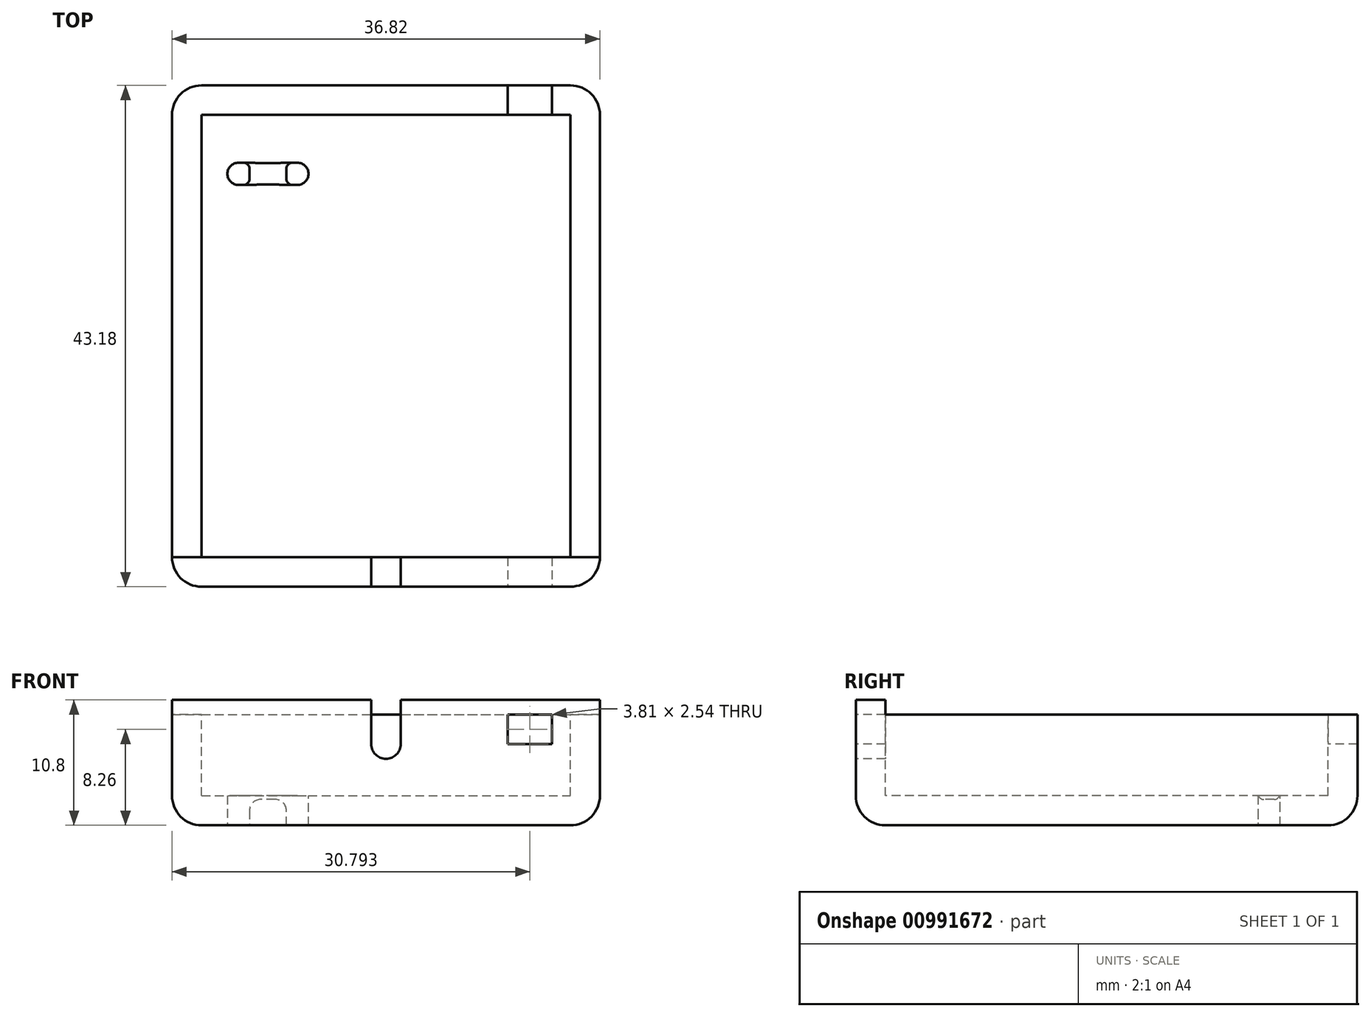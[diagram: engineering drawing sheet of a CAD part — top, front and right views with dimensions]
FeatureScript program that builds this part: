
annotation { "Feature Type Name" : "Feature", "Feature Type Description" : "" }
export const myFeature = defineFeature(function(context is Context, id is Id, definition is map)
    precondition{}
    {
        {
            var Q0;
            Q0=qCreatedBy(makeId("Top.planeOp"),FACE);
            var sketch = newSketch(context, id + "F0", { "sketchPlane" : qUnion([Q0])});
            skLineSegment(sketch, "E0.bottom", {"start": v(-18.42, 21.59) * mm, "end": v(18.42, 21.59) * mm});
            skLineSegment(sketch, "E0.top", {"start": v(-18.42, -21.6) * mm, "end": v(18.42, -21.6) * mm});
            skLineSegment(sketch, "E0.left", {"start": v(-18.42, 21.59) * mm, "end": v(-18.42, -21.6) * mm});
            skLineSegment(sketch, "E0.right", {"start": v(18.42, 21.59) * mm, "end": v(18.42, -21.6) * mm});
            skPoint(sketch, "E0.middle", {"position": v(0, 0) * mm});
            skSolve(sketch);
        }
        {
            var Q0;
            Q0 = qSketchRegion(id + "F0", true);
            extrude(context, id + "F1", {"entities" : qUnion([Q0]), "oppositeDirection" : true, "depth" : 9.52 * mm, "offsetDistance" : 25.4 * mm});
        }
        {
            var Q0;
            Q0=makeQuery(id+"F1.opExtrude","CAP_FACE",FACE,{"disambiguationData":[OSD([sQuery(id+"F0.wireOp",EDGE,"E0.bottom"),sQuery(id+"F0.wireOp",EDGE,"E0.top"),sQuery(id+"F0.wireOp",EDGE,"E0.left"),sQuery(id+"F0.wireOp",EDGE,"E0.right")])],"isStart":true});
            shell(context, id + "F2", {"entities" : qUnion([Q0]), "thickness" : 2.54 * mm});
        }
        {
            var Q0;
            Q0=makeQuery(id+"F1.opExtrude","CAP_FACE",FACE,{"disambiguationData":[OSD([sQuery(id+"F0.wireOp",EDGE,"E0.bottom"),sQuery(id+"F0.wireOp",EDGE,"E0.top"),sQuery(id+"F0.wireOp",EDGE,"E0.left"),sQuery(id+"F0.wireOp",EDGE,"E0.right")])],"isStart":true});
            var sketch = newSketch(context, id + "F3", { "sketchPlane" : qUnion([Q0])});
            skLineSegment(sketch, "E1.bottom", {"start": v(-18.42, -21.6) * mm, "end": v(18.42, -21.6) * mm});
            skLineSegment(sketch, "E1.top", {"start": v(-18.42, -19.05) * mm, "end": v(18.42, -19.05) * mm});
            skLineSegment(sketch, "E1.left", {"start": v(-18.42, -21.6) * mm, "end": v(-18.42, -19.05) * mm});
            skLineSegment(sketch, "E1.right", {"start": v(18.42, -21.6) * mm, "end": v(18.42, -19.05) * mm});
            skSolve(sketch);
        }
        {
            var Q0;
            Q0 = qSketchRegion(id + "F3", true);
            extrude(context, id + "F4", {"entities" : qUnion([Q0]), "operationType" : NewBodyOperationType.ADD, "depth" : 1.27 * mm, "offsetDistance" : 25.4 * mm});
        }
        {
            var Q0;
            Q0=makeQuery(id+"F4.boolean.opBoolean","MERGE",FACE,{"derivedFrom":[makeQuery(id+"F1.opExtrude","SWEPT_FACE",FACE,{"disambiguationData":[OSD([sQuery(id+"F0.wireOp",EDGE,"E0.top")])]}),makeQuery(id+"F4.opExtrude","SWEPT_FACE",FACE,{"disambiguationData":[OSD([sQuery(id+"F3.wireOp",EDGE,"E1.bottom")])]})]});
            var sketch = newSketch(context, id + "F5", { "sketchPlane" : qUnion([Q0])});
            skLineSegment(sketch, "E2", {"start": v(0, 1.27) * mm, "end": v(0, 0) * mm, "construction": true});
            skPoint(sketch, "E2.endSnap0", {"position": v(0, 1.27) * mm});
            skLineSegment(sketch, "E3", {"start": v(-10.48, 0) * mm, "end": v(10.48, 0) * mm, "construction": true});
            skLineSegment(sketch, "E4.bottom", {"start": v(10.48, 0) * mm, "end": v(14.29, 0) * mm});
            skLineSegment(sketch, "E4.top", {"start": v(10.48, -2.54) * mm, "end": v(14.29, -2.54) * mm});
            skLineSegment(sketch, "E4.left", {"start": v(10.48, 0) * mm, "end": v(10.48, -2.54) * mm});
            skLineSegment(sketch, "E4.right", {"start": v(14.29, 0) * mm, "end": v(14.29, -2.54) * mm});
            skSolve(sketch);
        }
        {
            var Q0;
            Q0=makeQuery(id+"F5.imprint","IMPRINT",FACE,{"disambiguationData":[TD([[makeQuery(id+"F5.imprint","IMPRINT",EDGE,{"derivedFrom":sQuery(id+"F5.wireOp",EDGE,"E4.bottom")}),-1.0]])]});
            extrude(context, id + "F6", {"entities" : qUnion([Q0]), "operationType" : NewBodyOperationType.REMOVE, "endBound" : BoundingType.THROUGH_ALL, "oppositeDirection" : true, "depth" : 25.4 * mm, "offsetDistance" : 25.4 * mm});
        }
        {
            var Q0;
            Q0=makeQuery(id+"F4.boolean.opBoolean","MERGE",EDGE,{"derivedFrom":[makeQuery(id+"F1.opExtrude","SWEPT_EDGE",EDGE,{"disambiguationData":[OSD([sQuery(id+"F0.wireOp",EDGE,"E0.top"),sQuery(id+"F0.wireOp",EDGE,"E0.right")])]}),makeQuery(id+"F4.opExtrude","SWEPT_EDGE",EDGE,{"disambiguationData":[OSD([sQuery(id+"F3.wireOp",EDGE,"E1.bottom"),sQuery(id+"F3.wireOp",EDGE,"E1.right")])]})]});
            var Q1;
            Q1=makeQuery(id+"F1.opExtrude","CAP_EDGE",EDGE,{"disambiguationData":[OSD([sQuery(id+"F0.wireOp",EDGE,"E0.right")])],"isStart":false});
            var Q2;
            Q2=makeQuery(id+"F1.opExtrude","CAP_EDGE",EDGE,{"disambiguationData":[OSD([sQuery(id+"F0.wireOp",EDGE,"E0.top")])],"isStart":false});
            var Q3;
            Q3=makeQuery(id+"F4.boolean.opBoolean","MERGE",EDGE,{"derivedFrom":[makeQuery(id+"F1.opExtrude","SWEPT_EDGE",EDGE,{"disambiguationData":[OSD([sQuery(id+"F0.wireOp",EDGE,"E0.top"),sQuery(id+"F0.wireOp",EDGE,"E0.left")])]}),makeQuery(id+"F4.opExtrude","SWEPT_EDGE",EDGE,{"disambiguationData":[OSD([sQuery(id+"F3.wireOp",EDGE,"E1.bottom"),sQuery(id+"F3.wireOp",EDGE,"E1.left")])]})]});
            var Q4;
            Q4=makeQuery(id+"F1.opExtrude","CAP_EDGE",EDGE,{"disambiguationData":[OSD([sQuery(id+"F0.wireOp",EDGE,"E0.left")])],"isStart":false});
            var Q5;
            Q5=makeQuery(id+"F3Qj1YdDXKK0PNa_1.1.F4.boolean.opBoolean","MERGE",EDGE,{"derivedFrom":[makeQuery(id+"F1.opExtrude","SWEPT_EDGE",EDGE,{"disambiguationData":[OSD([sQuery(id+"F0.wireOp",EDGE,"E0.bottom"),sQuery(id+"F0.wireOp",EDGE,"E0.left")])]}),makeQuery(id+"F3Qj1YdDXKK0PNa_1.1.F4.opExtrude","SWEPT_EDGE",EDGE,{"disambiguationData":[OSD([sQuery(id+"F3.wireOp",EDGE,"E1.bottom"),sQuery(id+"F3.wireOp",EDGE,"E1.left")])]})]});
            var Q6;
            Q6=makeQuery(id+"F3Qj1YdDXKK0PNa_1.1.F4.boolean.opBoolean","MERGE",EDGE,{"derivedFrom":[makeQuery(id+"F1.opExtrude","SWEPT_EDGE",EDGE,{"disambiguationData":[OSD([sQuery(id+"F0.wireOp",EDGE,"E0.bottom"),sQuery(id+"F0.wireOp",EDGE,"E0.left")])]}),makeQuery(id+"F3Qj1YdDXKK0PNa_1.1.F4.opExtrude","SWEPT_EDGE",EDGE,{"disambiguationData":[OSD([sQuery(id+"F3.wireOp",EDGE,"E1.bottom"),sQuery(id+"F3.wireOp",EDGE,"E1.left")])]})]});
            var Q7;
            Q7=makeQuery(id+"F1.opExtrude","CAP_EDGE",EDGE,{"disambiguationData":[OSD([sQuery(id+"F0.wireOp",EDGE,"E0.bottom")])],"isStart":false});
            var Q8;
            Q8=makeQuery(id+"F3Qj1YdDXKK0PNa_1.1.F4.boolean.opBoolean","MERGE",EDGE,{"derivedFrom":[makeQuery(id+"F1.opExtrude","SWEPT_EDGE",EDGE,{"disambiguationData":[OSD([sQuery(id+"F0.wireOp",EDGE,"E0.bottom"),sQuery(id+"F0.wireOp",EDGE,"E0.right")])]}),makeQuery(id+"F3Qj1YdDXKK0PNa_1.1.F4.opExtrude","SWEPT_EDGE",EDGE,{"disambiguationData":[OSD([sQuery(id+"F3.wireOp",EDGE,"E1.bottom"),sQuery(id+"F3.wireOp",EDGE,"E1.right")])]})]});
            fillet(context, id + "F7", {"entities" : qUnion([Q0, Q1, Q2, Q3, Q4, Q5, Q6, Q7, Q8]), "radius" : 2.54 * mm, "tangentPropagation" : true, "allowEdgeOverflow" : false});
        }
        {
            var Q0;
            Q0=makeQuery(id+"F4.boolean.opBoolean","MERGE",FACE,{"derivedFrom":[makeQuery(id+"F1.opExtrude","SWEPT_FACE",FACE,{"disambiguationData":[OSD([sQuery(id+"F0.wireOp",EDGE,"E0.top")])]}),makeQuery(id+"F4.opExtrude","SWEPT_FACE",FACE,{"disambiguationData":[OSD([sQuery(id+"F3.wireOp",EDGE,"E1.bottom")])]})]});
            var sketch = newSketch(context, id + "F8", { "sketchPlane" : qUnion([Q0])});
            skLineSegment(sketch, "E5.bottom", {"start": v(-1.27, 1.27) * mm, "end": v(1.27, 1.27) * mm});
            skLineSegment(sketch, "E5.top", {"start": v(-1.27, -2.54) * mm, "end": v(1.27, -2.54) * mm, "construction": true});
            skLineSegment(sketch, "E5.left", {"start": v(-1.27, 1.27) * mm, "end": v(-1.27, -2.54) * mm});
            skLineSegment(sketch, "E5.right", {"start": v(1.27, 1.27) * mm, "end": v(1.27, -2.54) * mm});
            skArc(sketch, "E6", {"start": v(1.27, -2.54) * mm, "mid": v(0, -3.81) * mm, "end": v(-1.27, -2.54) * mm});
            skLineSegment(sketch, "E7", {"start": v(0, 1.27) * mm, "end": v(0, 0) * mm, "construction": true});
            skLineSegment(sketch, "E8", {"start": v(1.27, -2.54) * mm, "end": v(10.48, -2.54) * mm, "construction": true});
            skSolve(sketch);
        }
        {
            var Q0;
            Q0 = qSketchRegion(id + "F8", true);
            extrude(context, id + "F9", {"entities" : qUnion([Q0]), "operationType" : NewBodyOperationType.REMOVE, "endBound" : BoundingType.UP_TO_NEXT, "oppositeDirection" : true, "depth" : 25.4 * mm, "offsetDistance" : 25.4 * mm});
        }
        {
            var Q0;
            Q0=makeQuery(id+"F3Qj1YdDXKK0PNa_1.1.F4.boolean.opBoolean","MERGE",FACE,{"derivedFrom":[makeQuery(id+"F2.opShell","OFFSET_FACE",FACE,{"disambiguationData":[OSD([sQuery(id+"F0.wireOp",EDGE,"E0.bottom")])]}),makeQuery(id+"F3Qj1YdDXKK0PNa_1.1.F4.opExtrude","SWEPT_FACE",FACE,{"disambiguationData":[OSD([sQuery(id+"F3.wireOp",EDGE,"E1.top")])]})]});
            cPlane(context, id + "F10", {"entities" : qUnion([Q0]), "cplaneType" : CPlaneType.OFFSET, "offset" : 5.08 * mm, "width" : 152.4 * mm, "height" : 152.4 * mm});
        }
        {
            var Q0;
            Q0=qCreatedBy(id+"F10.planeOp",FACE);
            var sketch = newSketch(context, id + "F11", { "sketchPlane" : qUnion([Q0])});
            skLineSegment(sketch, "E9.0", {"start": v(-15.88, -6.99) * mm, "end": v(15.88, -6.99) * mm, "construction": true});
            skLineSegment(sketch, "E10.0", {"start": v(-15.88, -9.53) * mm, "end": v(15.88, -9.53) * mm, "construction": true});
            skLineSegment(sketch, "E11", {"start": v(-7.62, -9.53) * mm, "end": v(-7.62, -8.26) * mm});
            skLineSegment(sketch, "E12", {"start": v(-12.7, -9.53) * mm, "end": v(-12.7, -8.26) * mm});
            skLineSegment(sketch, "E13", {"start": v(0, -6.99) * mm, "end": v(0, -13.56) * mm, "construction": true});
            skLineSegment(sketch, "E14", {"start": v(0, -13.56) * mm, "end": v(-10.16, -13.56) * mm, "construction": true});
            skLineSegment(sketch, "E15", {"start": v(-9.53, -6.35) * mm, "end": v(-10.8, -6.35) * mm});
            skArc(sketch, "E16", {"start": v(-7.62, -8.26) * mm, "mid": v(-8.18, -6.9) * mm, "end": v(-9.53, -6.35) * mm});
            skArc(sketch, "E17", {"start": v(-10.8, -6.35) * mm, "mid": v(-12.14, -6.9) * mm, "end": v(-12.7, -8.26) * mm});
            skLineSegment(sketch, "E18", {"start": v(-10.16, -6.35) * mm, "end": v(-10.16, -13.56) * mm, "construction": true});
            skLineSegment(sketch, "E19", {"start": v(-10.8, -5.4) * mm, "end": v(-10.8, -7.3) * mm, "construction": true});
            skSolve(sketch);
        }
        {
            var Q0;
            Q0=makeQuery(id+"F1.opExtrude","CAP_FACE",FACE,{"disambiguationData":[OSD([sQuery(id+"F0.wireOp",EDGE,"E0.bottom"),sQuery(id+"F0.wireOp",EDGE,"E0.top"),sQuery(id+"F0.wireOp",EDGE,"E0.left"),sQuery(id+"F0.wireOp",EDGE,"E0.right")])],"isStart":false});
            var sketch = newSketch(context, id + "F12", { "sketchPlane" : qUnion([Q0])});
            skArc(sketch, "E20", {"start": v(-7.62, -14.92) * mm, "mid": v(-6.67, -13.97) * mm, "end": v(-7.62, -13.02) * mm});
            skLineSegment(sketch, "E21.bottom", {"start": v(-7.62, -14.92) * mm, "end": v(-8.06, -14.92) * mm});
            skLineSegment(sketch, "E21.top", {"start": v(-7.62, -13.02) * mm, "end": v(-8.06, -13.02) * mm});
            skLineSegment(sketch, "E21.left", {"start": v(-7.62, -14.92) * mm, "end": v(-7.62, -13.02) * mm, "construction": true});
            skLineSegment(sketch, "E21.right", {"start": v(-8.57, -14.41) * mm, "end": v(-8.57, -13.53) * mm});
            skPoint(sketch, "E22.visualSharp", {"position": v(-8.57, -14.92) * mm});
            skArc(sketch, "E22.filletArc", {"start": v(-8.57, -14.41) * mm, "mid": v(-8.42, -14.77) * mm, "end": v(-8.06, -14.92) * mm});
            skPoint(sketch, "E23.visualSharp", {"position": v(-8.57, -13.02) * mm});
            skArc(sketch, "E23.filletArc", {"start": v(-8.06, -13.02) * mm, "mid": v(-8.42, -13.17) * mm, "end": v(-8.57, -13.53) * mm});
            skSolve(sketch);
        }
        {
            var Q0;
            Q0=makeQuery(id+"F12.imprint","IMPRINT",FACE,{"disambiguationData":[TD([[makeQuery(id+"F12.imprint","IMPRINT",EDGE,{"derivedFrom":sQuery(id+"F12.wireOp",EDGE,"E20")}),1.0]])]});
            var Q1;
            Q1 = qSketchRegion(id + "F11", true);
            var Q2;
            Q2=sQuery(id+"F11.wireOp",EDGE,"E11");
            var Q3;
            Q3=sQuery(id+"F11.wireOp",EDGE,"E16");
            var Q4;
            Q4=sQuery(id+"F11.wireOp",EDGE,"E15");
            var Q5;
            Q5=sQuery(id+"F11.wireOp",EDGE,"E17");
            var Q6;
            Q6=sQuery(id+"F11.wireOp",EDGE,"E12");
            sweep(context, id + "F13", {"operationType" : NewBodyOperationType.REMOVE, "profiles" : qUnion([Q0, Q1]), "path" : qUnion([Q2, Q3, Q4, Q5, Q6])});
        }
        {
            var Q0;
            Q0=makeQuery(id+"F1.opExtrude","CAP_FACE",FACE,{"disambiguationData":[OSD([sQuery(id+"F0.wireOp",EDGE,"E0.bottom"),sQuery(id+"F0.wireOp",EDGE,"E0.top"),sQuery(id+"F0.wireOp",EDGE,"E0.left"),sQuery(id+"F0.wireOp",EDGE,"E0.right")])],"isStart":false});
            var sketch = newSketch(context, id + "F14", { "sketchPlane" : qUnion([Q0])});
            skLineSegment(sketch, "E24.0", {"start": v(-12.26, -13.02) * mm, "end": v(-12.7, -13.02) * mm});
            skLineSegment(sketch, "E24.1", {"start": v(-8.57, -14.41) * mm, "end": v(-8.57, -13.53) * mm});
            skLineSegment(sketch, "E24.2", {"start": v(-8.06, -13.02) * mm, "end": v(-7.62, -13.02) * mm});
            skArc(sketch, "E24.3", {"start": v(-12.7, -13.02) * mm, "mid": v(-13.65, -13.97) * mm, "end": v(-12.7, -14.92) * mm});
            skLineSegment(sketch, "E24.4", {"start": v(-12.7, -14.92) * mm, "end": v(-12.26, -14.92) * mm});
            skLineSegment(sketch, "E24.5", {"start": v(-7.62, -14.92) * mm, "end": v(-8.06, -14.92) * mm});
            skArc(sketch, "E24.6", {"start": v(-8.57, -13.53) * mm, "mid": v(-8.42, -13.17) * mm, "end": v(-8.06, -13.02) * mm});
            skArc(sketch, "E24.7", {"start": v(-12.26, -14.92) * mm, "mid": v(-11.9, -14.77) * mm, "end": v(-11.75, -14.41) * mm});
            skArc(sketch, "E24.8", {"start": v(-7.62, -13.02) * mm, "mid": v(-6.67, -13.97) * mm, "end": v(-7.62, -14.92) * mm});
            skArc(sketch, "E24.9", {"start": v(-8.06, -14.92) * mm, "mid": v(-8.42, -14.77) * mm, "end": v(-8.57, -14.41) * mm});
            skLineSegment(sketch, "E24.10", {"start": v(-11.75, -14.41) * mm, "end": v(-11.75, -13.53) * mm});
            skArc(sketch, "E24.11", {"start": v(-11.75, -13.53) * mm, "mid": v(-11.9, -13.17) * mm, "end": v(-12.26, -13.02) * mm});
            skSolve(sketch);
        }
        {
            var Q0;
            Q0 = qSketchRegion(id + "F14", true);
            extrude(context, id + "F15", {"entities" : qUnion([Q0]), "operationType" : NewBodyOperationType.REMOVE, "endBound" : BoundingType.THROUGH_ALL, "oppositeDirection" : true, "depth" : 25.4 * mm, "offsetDistance" : 25.4 * mm});
        }
    });
